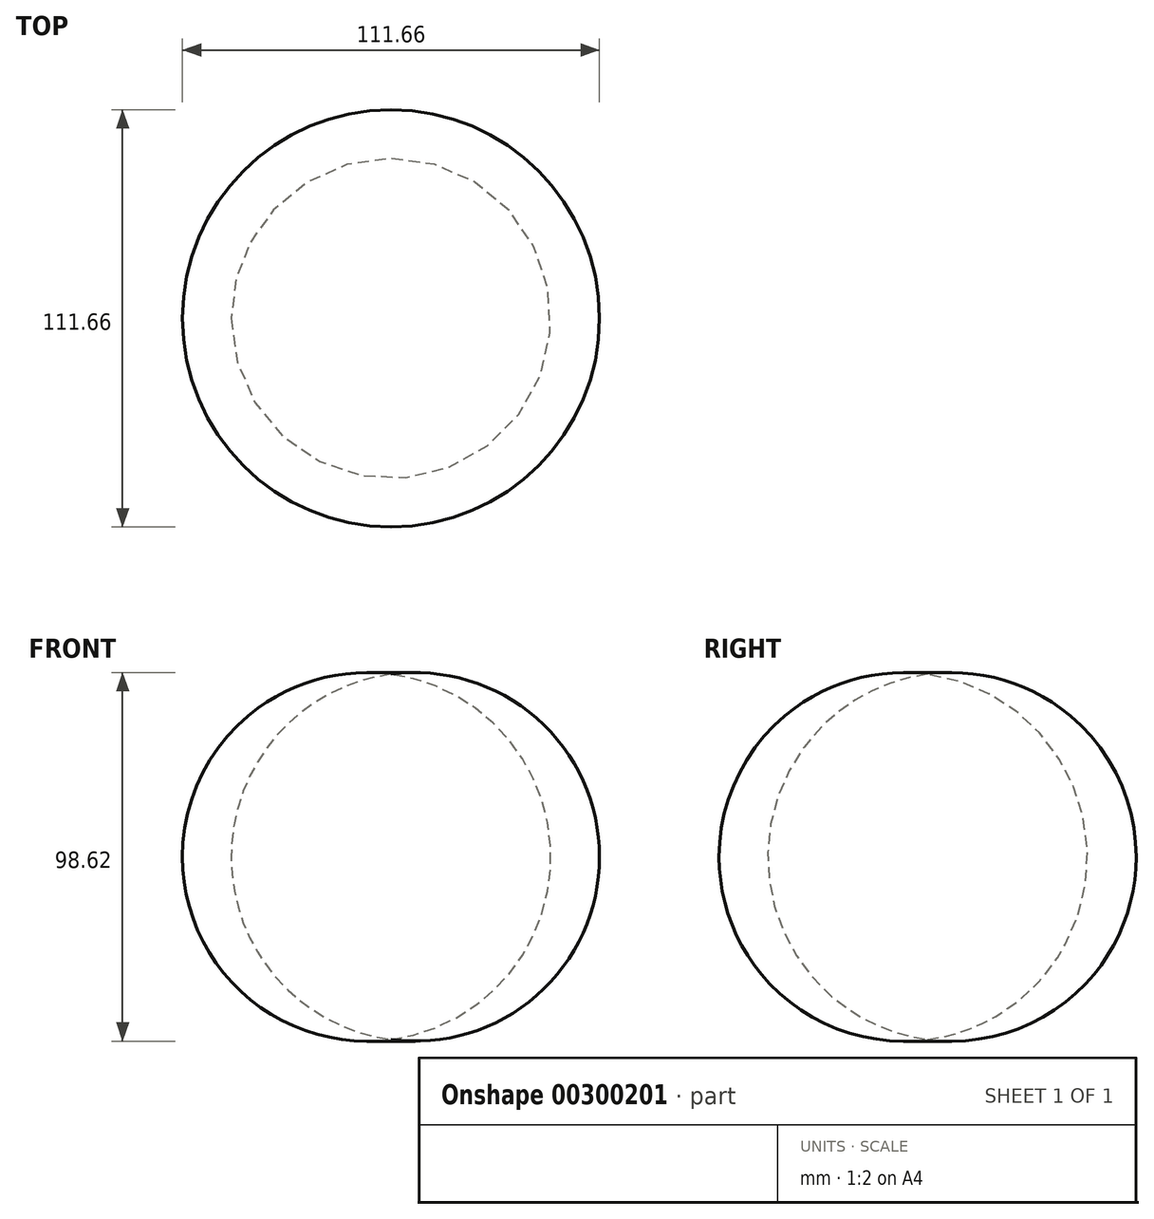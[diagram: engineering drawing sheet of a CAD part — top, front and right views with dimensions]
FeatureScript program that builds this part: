
annotation { "Feature Type Name" : "Feature", "Feature Type Description" : "" }
export const myFeature = defineFeature(function(context is Context, id is Id, definition is map)
    precondition{}
    {
        {
            var Q0;
            Q0=qCreatedBy(makeId("Front.planeOp"),FACE);
            var sketch = newSketch(context, id + "F0", { "sketchPlane" : qUnion([Q0])});
            skLineSegment(sketch, "E0", {"start": v(0, 52.94) * mm, "end": v(0, -44.82) * mm});
            skArc(sketch, "E1", {"start": v(0, -44.82) * mm, "mid": v(42.8, 4.06) * mm, "end": v(0, 52.94) * mm});
            skSolve(sketch);
        }
        {
            var Q0;
            Q0 = qSketchRegion(id + "F0", true);
            var Q1;
            Q1=sQuery(id+"F0.wireOp",EDGE,"E0");
            revolve(context, id + "F1", {"entities" : qUnion([Q0]), "axis" : qUnion([Q1]), "revolveType" : RevolveType.FULL});
        }
    });
